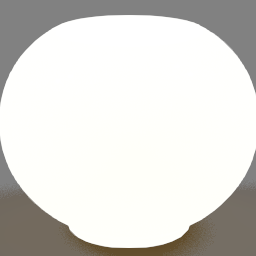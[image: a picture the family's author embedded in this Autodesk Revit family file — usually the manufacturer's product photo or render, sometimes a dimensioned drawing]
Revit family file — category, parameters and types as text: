
# Revit family: 3-060X-xx Starlight Mirror
name_source: partatom
category: Luminarias
units: mm (PartAtom-declared; Revit-internal decimal feet)

## family parameters
Anfitrión = Muro
Compartido = No
Corte con vacíos al cargar = No
Cota de conector redondo = Diámetro de uso
Número OmniClass = 23.80.70.00
Origen de luz = No
Punto de cálculo de habitación = No
Siempre vertical = Sí
Tipo de pieza = Normal
Título OmniClass = Lighting

## types (5) — shared parameters
Diffuser = Ghost Mirror
Fabricante = Vanita by Oxygen
Lámpara = LED Array
Metal Finish 1 = 15 - Black
Modelo = 3-060X-xx / Starlight
References = Ref. 3 = 120 V / Ref. 37 = 277 V
URL = www.oxygenlighting.com
Voltage = 120 V
Voltage Input = 120 V or 277 V - 50/60 Hz
zero-valued in all types: Elevación por defecto

## per-type parameters (varying)
| type | Comentarios de vataje | Height | Width |
| 3-0601-15 / Black | 1 x 60.9 W at 120 V | 914 mm  [stored 2.99869 ft] | 610 mm  [stored 2.00131 ft] |
| 3-0603-15 / Black | 1 x 88.2 W at 120 V | 914 mm  [stored 2.99869 ft] | 1219 mm |
| 3-0604-15 / Black | 1 x 123.3 W at 120 V | 1219 mm | 1219 mm |
| 3-0605-15 / Black | 1 x 126.3 W at 120 V | 1067 mm  [stored 3.50066 ft] | 1524 mm  [stored 5 ft] |
| 3-0602-15 / Black | 1 x 67.4 W at 120 V | 914 mm  [stored 2.99869 ft] | 914 mm  [stored 2.99869 ft] |

note: [stored X ft] marks values corroborated as IEEE doubles in the binary element streams (Revit-internal decimal feet)

## geometry (parser evidence)
native form markers: Sweep x6
no freeform markers — native parametric forms only
